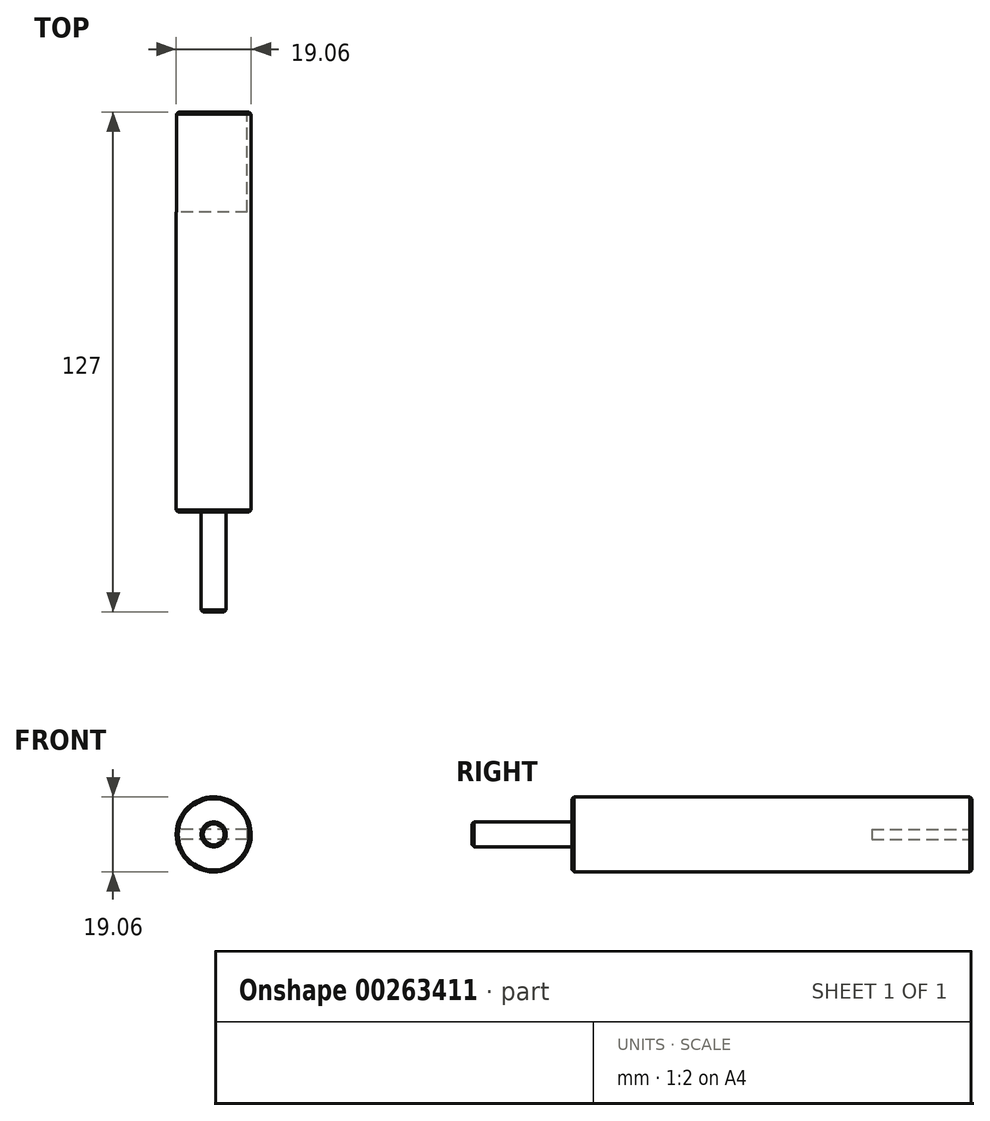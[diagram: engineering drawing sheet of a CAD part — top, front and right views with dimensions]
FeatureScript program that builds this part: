
annotation { "Feature Type Name" : "Feature", "Feature Type Description" : "" }
export const myFeature = defineFeature(function(context is Context, id is Id, definition is map)
    precondition{}
    {
        {
            var Q0;
            Q0=qCreatedBy(makeId("Front.planeOp"),FACE);
            var sketch = newSketch(context, id + "F0", { "sketchPlane" : qUnion([Q0])});
            skCircle(sketch, "E0", {"center": v(0, 0) * mm, "radius": 9.53 * mm});
            skSolve(sketch);
        }
        {
            var Q0;
            Q0 = qSketchRegion(id + "F0", true);
            extrude(context, id + "F1", {"entities" : qUnion([Q0]), "depth" : 101.6 * mm});
        }
        {
            var Q0;
            Q0=qCreatedBy(makeId("Front.planeOp"),FACE);
            var sketch = newSketch(context, id + "F2", { "sketchPlane" : qUnion([Q0])});
            skPoint(sketch, "E1.middle", {"position": v(0, 0) * mm});
            skLineSegment(sketch, "E2.bottom", {"start": v(0, 1.28) * mm, "end": v(-9.53, 1.28) * mm});
            skLineSegment(sketch, "E2.top", {"start": v(0, -1.28) * mm, "end": v(-9.53, -1.28) * mm});
            skLineSegment(sketch, "E2.left", {"start": v(0, 1.28) * mm, "end": v(0, -1.28) * mm});
            skLineSegment(sketch, "E2.right", {"start": v(-9.53, 1.28) * mm, "end": v(-9.53, -1.28) * mm});
            skLineSegment(sketch, "E3.bottom", {"start": v(0, 1.28) * mm, "end": v(8.52, 1.28) * mm});
            skLineSegment(sketch, "E3.top", {"start": v(0, -1.28) * mm, "end": v(8.52, -1.28) * mm});
            skLineSegment(sketch, "E3.right", {"start": v(8.52, 1.28) * mm, "end": v(8.52, -1.28) * mm});
            skSolve(sketch);
        }
        {
            var Q0;
            Q0 = qSketchRegion(id + "F2", true);
            extrude(context, id + "F3", {"entities" : qUnion([Q0]), "operationType" : NewBodyOperationType.REMOVE, "depth" : 25.4 * mm});
        }
        {
            var Q0;
            Q0=makeQuery(id+"F1.opExtrude","CAP_FACE",FACE,{"disambiguationData":[OSD([sQuery(id+"F0.wireOp",EDGE,"E0")])],"isStart":false});
            var sketch = newSketch(context, id + "F4", { "sketchPlane" : qUnion([Q0])});
            skCircle(sketch, "E4", {"center": v(0, 0) * mm, "radius": 3.18 * mm});
            skSolve(sketch);
        }
        {
            var Q0;
            Q0 = qSketchRegion(id + "F4", true);
            extrude(context, id + "F5", {"entities" : qUnion([Q0]), "operationType" : NewBodyOperationType.ADD, "depth" : 25.4 * mm, "offsetDistance" : 25.4 * mm});
        }
        {
            var Q0;
            Q0=makeQuery(id+"F5.opExtrude","CAP_EDGE",EDGE,{"disambiguationData":[OSD([sQuery(id+"F4.wireOp",EDGE,"E4")])],"isStart":false});
            var Q1;
            Q1=makeQuery(id+"F1.opExtrude","CAP_EDGE",EDGE,{"disambiguationData":[OSD([sQuery(id+"F0.wireOp",EDGE,"E0")])],"isStart":false});
            var Q2;
            Q2=makeQuery(id+"F1.opExtrude","CAP_EDGE",EDGE,{"disambiguationData":[OSD([sQuery(id+"F0.wireOp",EDGE,"E0")])],"isStart":true});
            chamfer(context, id + "F6", {"entities" : qUnion([Q0, Q1, Q2]), "width" : 0.5 * mm, "tangentPropagation" : true});
        }
    });
